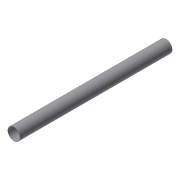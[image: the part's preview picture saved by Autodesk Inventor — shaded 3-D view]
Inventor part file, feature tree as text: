
AUTODESK INVENTOR PART (.ipt)
format: ipt  version: 2016 (Build 200138000, 138)  size: 71,168 bytes
history: native  units: in
note: dims shown in document units (in); Inventor stores cm internally (conversion verified against a paired STEP export)
features: extrude x1, sketch x1
ambient origin geometry x8: Origin, YZ Plane, XZ Plane, XY Plane, X Axis, Y Axis, Z Axis, Center Point
bodies: Solid1 (feature_tree)
feature tree (2):
  extrude  "Extrusion1"  Depth=53.0512in
  sketch  "Sketch1"  dims[d1=0.0906in d2=4.3307in d3=53.0512in d4=0.0in]
